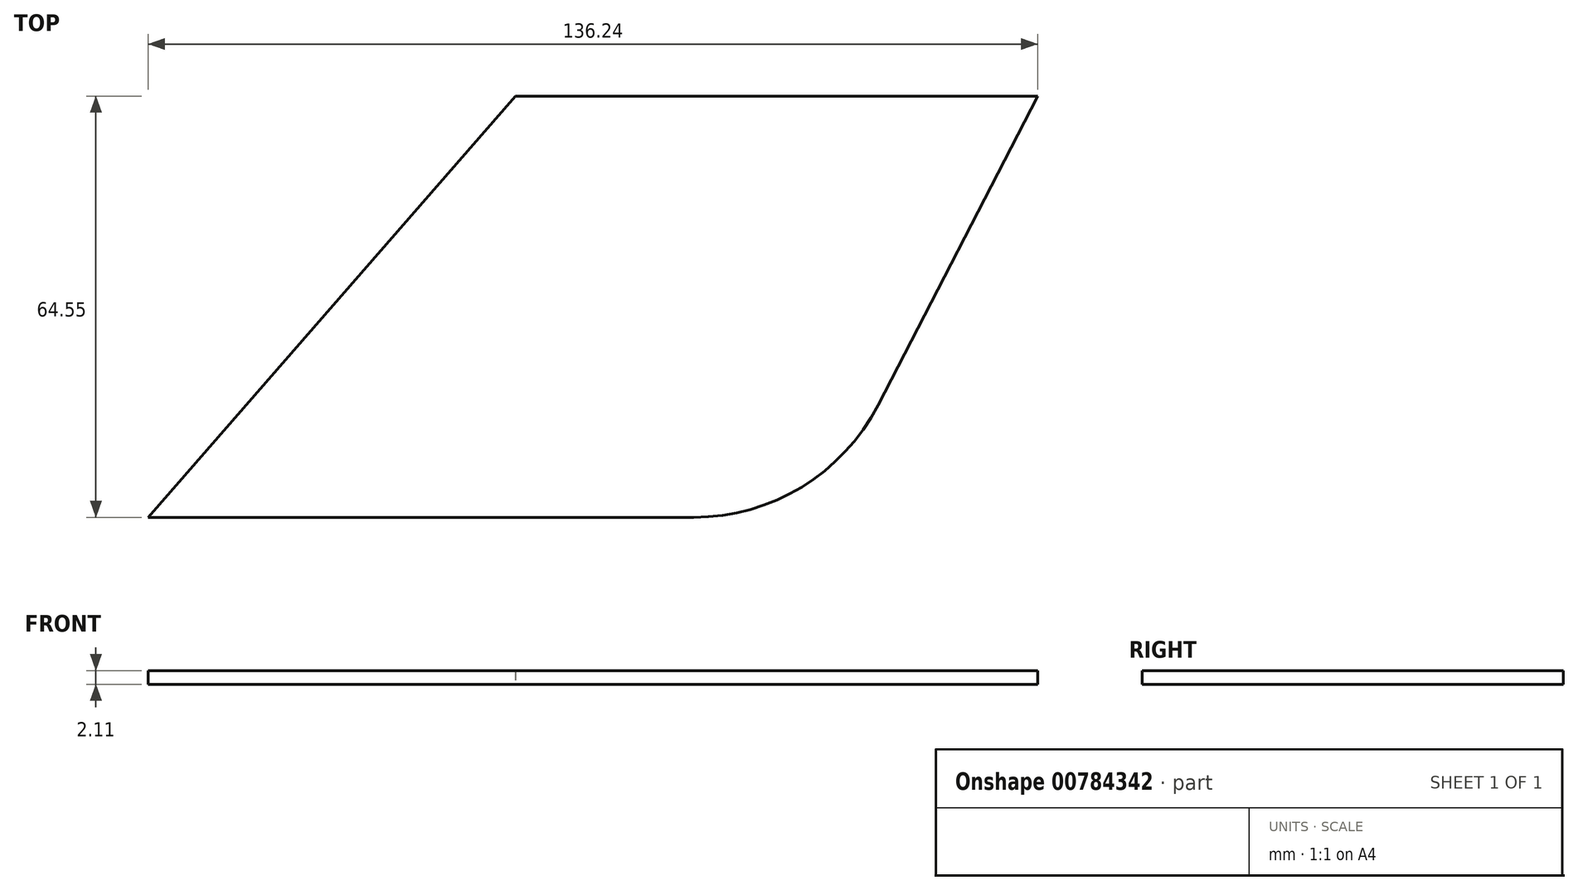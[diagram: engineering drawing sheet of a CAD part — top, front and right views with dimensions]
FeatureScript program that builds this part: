
annotation { "Feature Type Name" : "Feature", "Feature Type Description" : "" }
export const myFeature = defineFeature(function(context is Context, id is Id, definition is map)
    precondition{}
    {
        {
            var Q0;
            Q0=qCreatedBy(makeId("Top.planeOp"),FACE);
            var sketch = newSketch(context, id + "F0", { "sketchPlane" : qUnion([Q0])});
            skLineSegment(sketch, "E0.bottom", {"start": v(-5.7, 42.94) * mm, "end": v(54.3, 42.94) * mm});
            skLineSegment(sketch, "E0.top", {"start": v(-33.37, -21.61) * mm, "end": v(21.64, -21.61) * mm});
            skLineSegment(sketch, "E1", {"start": v(-33.37, -21.61) * mm, "end": v(-61.94, -21.61) * mm});
            skLineSegment(sketch, "E2", {"start": v(-61.94, -21.61) * mm, "end": v(-5.7, 42.94) * mm});
            skLineSegment(sketch, "E3", {"start": v(54.3, 42.94) * mm, "end": v(74.3, 42.94) * mm});
            skLineSegment(sketch, "E4", {"start": v(74.3, 42.94) * mm, "end": v(49.85, -4.42) * mm});
            skPoint(sketch, "E5.visualSharp", {"position": v(40.98, -21.61) * mm});
            skArc(sketch, "E5.filletArc", {"start": v(21.64, -21.61) * mm, "mid": v(38.16, -16.98) * mm, "end": v(49.85, -4.42) * mm});
            skSolve(sketch);
        }
        {
            var Q0;
            Q0=makeQuery(id+"F0.imprint","IMPRINT",FACE,{"disambiguationData":[TD([[makeQuery(id+"F0.imprint","IMPRINT",EDGE,{"derivedFrom":sQuery(id+"F0.wireOp",EDGE,"E0.bottom")}),-1.0]])]});
            extrude(context, id + "F1", {"entities" : qUnion([Q0]), "depth" : 2.1 * mm, "offsetDistance" : 25.4 * mm});
        }
    });
